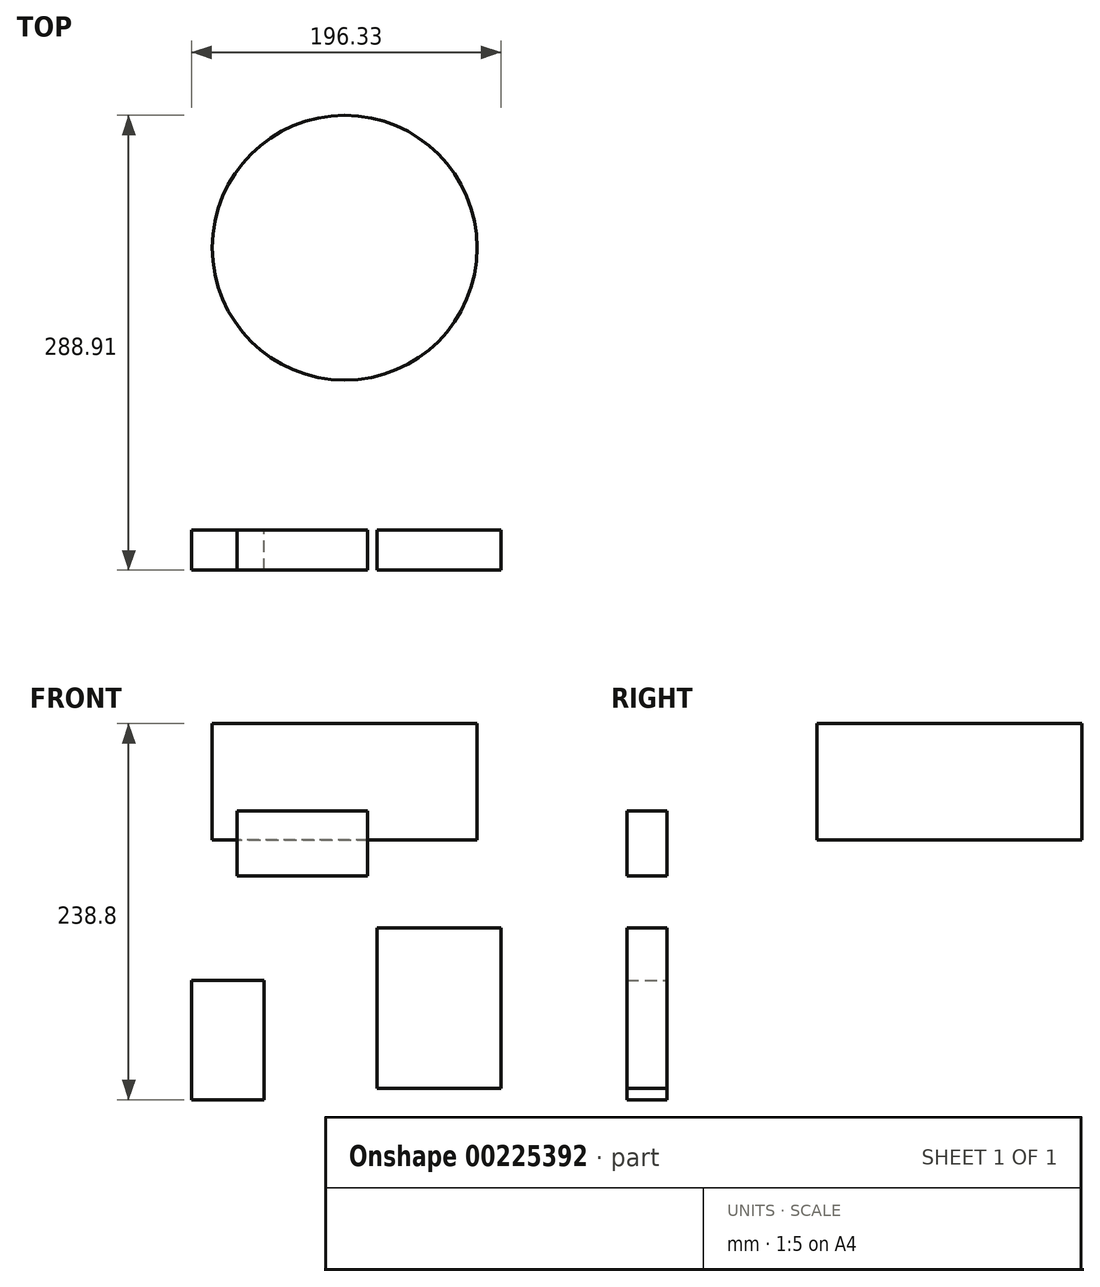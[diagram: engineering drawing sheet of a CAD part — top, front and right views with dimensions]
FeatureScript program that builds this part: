
annotation { "Feature Type Name" : "Feature", "Feature Type Description" : "" }
export const myFeature = defineFeature(function(context is Context, id is Id, definition is map)
    precondition{}
    {
        {
            var Q0;
            Q0=qCreatedBy(makeId("Front.planeOp"),FACE);
            var sketch = newSketch(context, id + "F1", { "sketchPlane" : qUnion([Q0])});
            skLineSegment(sketch, "E0.bottom", {"start": v(-68.37, 133.93) * mm, "end": v(14.6, 133.93) * mm});
            skLineSegment(sketch, "E0.top", {"start": v(-68.37, 92.48) * mm, "end": v(14.6, 92.48) * mm});
            skLineSegment(sketch, "E0.left", {"start": v(-68.37, 133.93) * mm, "end": v(-68.37, 92.48) * mm});
            skLineSegment(sketch, "E0.right", {"start": v(14.6, 133.93) * mm, "end": v(14.6, 92.48) * mm});
            skLineSegment(sketch, "E1.bottom", {"start": v(-97.16, 26.14) * mm, "end": v(-51.22, 26.14) * mm});
            skLineSegment(sketch, "E1.top", {"start": v(-97.16, -49.5) * mm, "end": v(-51.22, -49.5) * mm});
            skLineSegment(sketch, "E1.left", {"start": v(-97.16, 26.14) * mm, "end": v(-97.16, -49.5) * mm});
            skLineSegment(sketch, "E1.right", {"start": v(-51.22, 26.14) * mm, "end": v(-51.22, -49.5) * mm});
            skLineSegment(sketch, "E2.bottom", {"start": v(20.53, 59.7) * mm, "end": v(99.17, 59.7) * mm});
            skLineSegment(sketch, "E2.top", {"start": v(20.53, -42.39) * mm, "end": v(99.17, -42.39) * mm});
            skLineSegment(sketch, "E2.left", {"start": v(20.53, 59.7) * mm, "end": v(20.53, -42.39) * mm});
            skLineSegment(sketch, "E2.right", {"start": v(99.17, 59.7) * mm, "end": v(99.17, -42.39) * mm});
            skSolve(sketch);
        }
        {
            var Q0;
            Q0 = qSketchRegion(id + "F1", true);
            extrude(context, id + "F2", {"entities" : qUnion([Q0]), "depth" : 25.4 * mm});
        }
        {
            var Q0;
            Q0=qCreatedBy(makeId("Right.planeOp"),FACE);
            var sketch = newSketch(context, id + "F3", { "sketchPlane" : qUnion([Q0])});
            skLineSegment(sketch, "E3.bottom", {"start": v(179.41, 115.36) * mm, "end": v(263.51, 115.36) * mm});
            skLineSegment(sketch, "E3.top", {"start": v(179.41, 189.3) * mm, "end": v(263.51, 189.3) * mm});
            skLineSegment(sketch, "E3.left", {"start": v(179.41, 115.36) * mm, "end": v(179.41, 189.3) * mm});
            skLineSegment(sketch, "E3.right", {"start": v(263.51, 115.36) * mm, "end": v(263.51, 189.3) * mm});
            skSolve(sketch);
        }
        {
            var Q0;
            Q0 = qSketchRegion(id + "F3", true);
            var Q1;
            Q1=sQuery(id+"F3.wireOp",EDGE,"E3.left");
            revolve(context, id + "F0", {"entities" : qUnion([Q0]), "axis" : qUnion([Q1]), "revolveType" : RevolveType.FULL});
        }
    });
